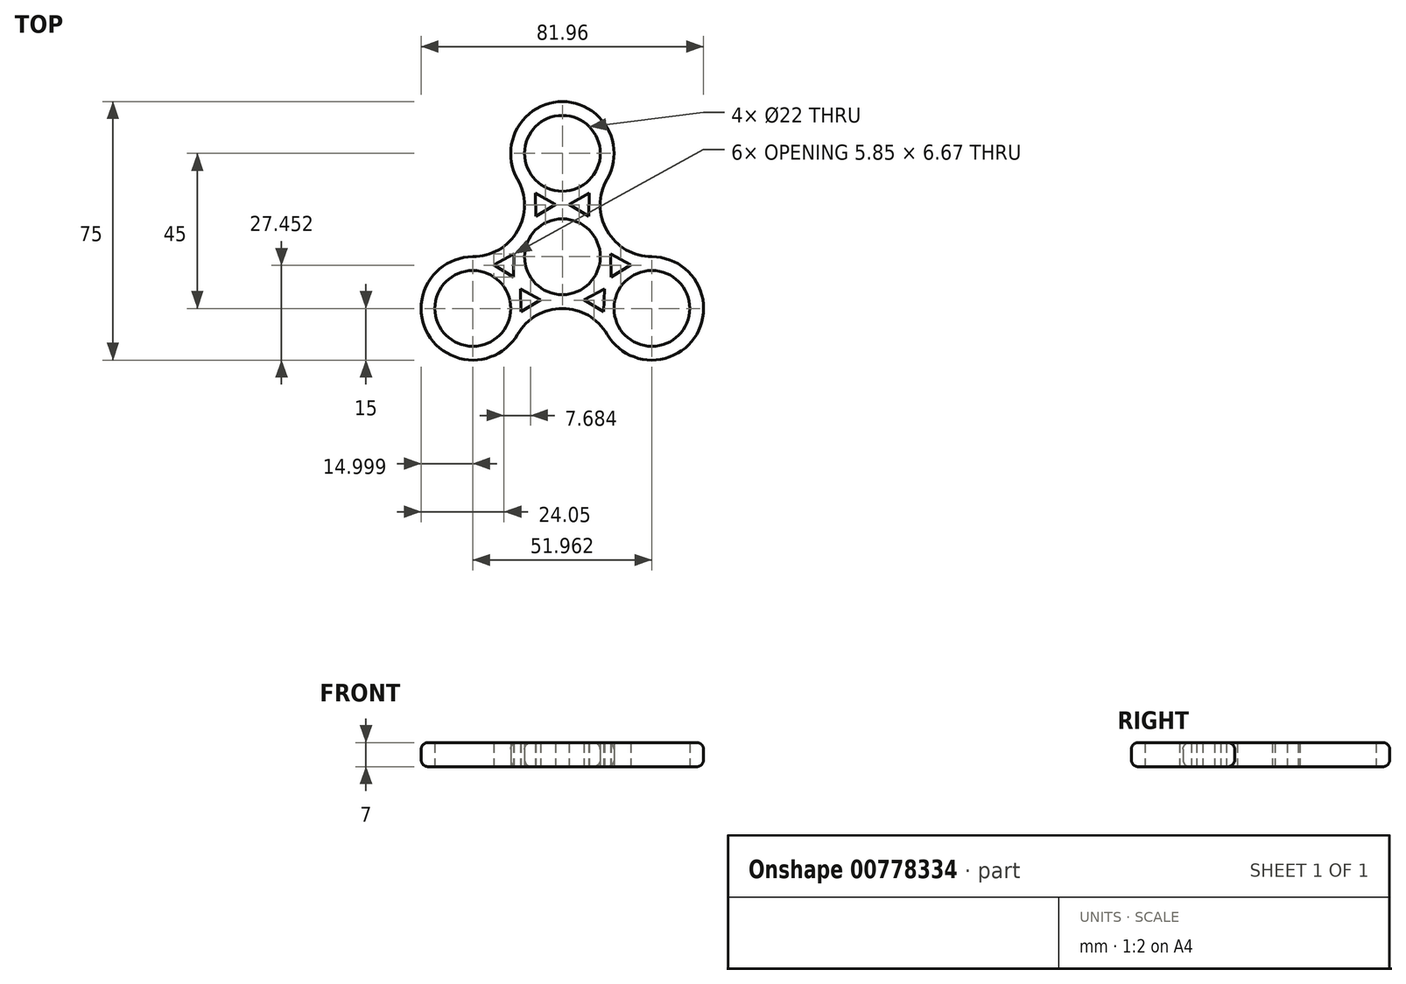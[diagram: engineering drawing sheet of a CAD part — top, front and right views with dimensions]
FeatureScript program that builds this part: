
annotation { "Feature Type Name" : "Feature", "Feature Type Description" : "" }
export const myFeature = defineFeature(function(context is Context, id is Id, definition is map)
    precondition{}
    {
        {
            var Q0;
            Q0=qCreatedBy(makeId("Top.planeOp"),FACE);
            var sketch = newSketch(context, id + "F0", { "sketchPlane" : qUnion([Q0])});
            skCircle(sketch, "E0", {"center": v(0, 0) * mm, "radius": 11 * mm});
            skCircle(sketch, "E1", {"center": v(0, 30) * mm, "radius": 11 * mm});
            skCircle(sketch, "E2", {"center": v(0, 0) * mm, "radius": 30 * mm, "construction": true});
            skLineSegment(sketch, "E3.0", {"start": v(0, 30) * mm, "end": v(25.98, -15) * mm, "construction": true});
            skLineSegment(sketch, "E3.1", {"start": v(25.98, -15) * mm, "end": v(-25.98, -15) * mm, "construction": true});
            skLineSegment(sketch, "E3.2", {"start": v(-25.98, -15) * mm, "end": v(0, 30) * mm, "construction": true});
            skCircle(sketch, "E4", {"center": v(-25.98, -15) * mm, "radius": 11 * mm});
            skCircle(sketch, "E5", {"center": v(25.98, -15) * mm, "radius": 11 * mm});
            skCircle(sketch, "E6", {"center": v(0, 0) * mm, "radius": 15 * mm, "construction": true});
            skArc(sketch, "E7", {"start": v(13, 22.5) * mm, "mid": v(0, 45) * mm, "end": v(-13, 22.5) * mm});
            skArc(sketch, "E8", {"start": v(13, -22.5) * mm, "mid": v(38.97, -22.5) * mm, "end": v(25.98, 0) * mm});
            skArc(sketch, "E9", {"start": v(-25.98, 0) * mm, "mid": v(-38.97, -22.5) * mm, "end": v(-13, -22.5) * mm});
            skArc(sketch, "E10", {"start": v(-25.98, 0) * mm, "mid": v(-13, 7.5) * mm, "end": v(-13, 22.5) * mm});
            skLineSegment(sketch, "E11", {"start": v(25.98, -15) * mm, "end": v(0, 0) * mm, "construction": true});
            skLineSegment(sketch, "E12", {"start": v(0, 0) * mm, "end": v(-35.55, 20.52) * mm, "construction": true});
            skLineSegment(sketch, "E13", {"start": v(-25.98, -15) * mm, "end": v(0, 0) * mm, "construction": true});
            skLineSegment(sketch, "E14", {"start": v(0, 0) * mm, "end": v(34.88, 20.14) * mm, "construction": true});
            skArc(sketch, "E15", {"start": v(13, 22.5) * mm, "mid": v(13, 7.5) * mm, "end": v(25.98, 0) * mm});
            skArc(sketch, "E16", {"start": v(13, -22.5) * mm, "mid": v(0, -15) * mm, "end": v(-13, -22.5) * mm});
            skCircle(sketch, "E17", {"center": v(0, 0) * mm, "radius": 16.75 * mm, "construction": true});
            skLineSegment(sketch, "E18.0", {"start": v(-7.83, 18.4) * mm, "end": v(-1.98, 15.2) * mm});
            skLineSegment(sketch, "E18.1", {"start": v(-1.98, 15.2) * mm, "end": v(-7.68, 11.74) * mm});
            skLineSegment(sketch, "E18.2", {"start": v(-7.68, 11.74) * mm, "end": v(-7.83, 18.4) * mm});
            skPoint(sketch, "E19.orphan", {"position": v(1.38, 16.14) * mm});
            skPoint(sketch, "E20.orphan", {"position": v(14.66, -6.88) * mm});
            skPoint(sketch, "E21.orphan", {"position": v(13.29, -9.26) * mm});
            skPoint(sketch, "E22.orphan", {"position": v(-14.66, -6.88) * mm});
            skPoint(sketch, "E23.orphan", {"position": v(-13.29, -9.26) * mm});
            skLineSegment(sketch, "E24.MirrorCS", {"start": v(7.83, 18.4) * mm, "end": v(1.98, 15.2) * mm});
            skLineSegment(sketch, "E25.MirrorCS", {"start": v(7.68, 11.74) * mm, "end": v(7.83, 18.4) * mm});
            skLineSegment(sketch, "E26.MirrorCS", {"start": v(1.98, 15.2) * mm, "end": v(7.68, 11.74) * mm});
            skLineSegment(sketch, "E27.MirrorCS", {"start": v(14, 0.79) * mm, "end": v(19.85, -2.42) * mm});
            skLineSegment(sketch, "E28.MirrorCS", {"start": v(14.15, -5.88) * mm, "end": v(14, 0.79) * mm});
            skLineSegment(sketch, "E29.MirrorCS", {"start": v(19.85, -2.42) * mm, "end": v(14.15, -5.88) * mm});
            skLineSegment(sketch, "E30.MirrorCS", {"start": v(12.17, -9.31) * mm, "end": v(6.32, -12.52) * mm});
            skLineSegment(sketch, "E31.MirrorCS", {"start": v(12.03, -15.98) * mm, "end": v(12.17, -9.31) * mm});
            skLineSegment(sketch, "E32.MirrorCS", {"start": v(6.32, -12.52) * mm, "end": v(12.03, -15.98) * mm});
            skLineSegment(sketch, "E33.MirrorCS", {"start": v(-14.15, -5.88) * mm, "end": v(-14, 0.79) * mm});
            skLineSegment(sketch, "E34.MirrorCS", {"start": v(-14, 0.79) * mm, "end": v(-19.85, -2.42) * mm});
            skLineSegment(sketch, "E35.MirrorCS", {"start": v(-19.85, -2.42) * mm, "end": v(-14.15, -5.88) * mm});
            skLineSegment(sketch, "E36.MirrorCS", {"start": v(-12.17, -9.31) * mm, "end": v(-6.32, -12.52) * mm});
            skLineSegment(sketch, "E37.MirrorCS", {"start": v(-12.03, -15.98) * mm, "end": v(-12.17, -9.31) * mm});
            skLineSegment(sketch, "E38.MirrorCS", {"start": v(-6.32, -12.52) * mm, "end": v(-12.03, -15.98) * mm});
            skSolve(sketch);
        }
        {
            var Q0;
            Q0=makeQuery(id+"F0.imprint","IMPRINT",FACE,{"disambiguationData":[TD([[makeQuery(id+"F0.imprint","IMPRINT",EDGE,{"derivedFrom":sQuery(id+"F0.wireOp",EDGE,"E0")}),-1.0]])]});
            extrude(context, id + "F1", {"entities" : qUnion([Q0]), "depth" : 7 * mm, "offsetDistance" : 25 * mm});
        }
        {
            var Q0;
            Q0=makeQuery(id+"F1.opExtrude","CAP_EDGE",EDGE,{"disambiguationData":[OSD([sQuery(id+"F0.wireOp",EDGE,"E10")])],"isStart":false});
            var Q1;
            Q1=makeQuery(id+"F1.opExtrude","CAP_EDGE",EDGE,{"disambiguationData":[OSD([sQuery(id+"F0.wireOp",EDGE,"E7")])],"isStart":false});
            var Q2;
            Q2=makeQuery(id+"F1.opExtrude","CAP_EDGE",EDGE,{"disambiguationData":[OSD([sQuery(id+"F0.wireOp",EDGE,"E15")])],"isStart":true});
            var Q3;
            Q3=makeQuery(id+"F1.opExtrude","CAP_EDGE",EDGE,{"disambiguationData":[OSD([sQuery(id+"F0.wireOp",EDGE,"E15")])],"isStart":false});
            var Q4;
            Q4=makeQuery(id+"F1.opExtrude","CAP_EDGE",EDGE,{"disambiguationData":[OSD([sQuery(id+"F0.wireOp",EDGE,"E8")])],"isStart":false});
            var Q5;
            Q5=makeQuery(id+"F1.opExtrude","CAP_EDGE",EDGE,{"disambiguationData":[OSD([sQuery(id+"F0.wireOp",EDGE,"E16")])],"isStart":false});
            var Q6;
            Q6=makeQuery(id+"F1.opExtrude","CAP_EDGE",EDGE,{"disambiguationData":[OSD([sQuery(id+"F0.wireOp",EDGE,"E9")])],"isStart":false});
            var Q7;
            Q7=makeQuery(id+"F1.opExtrude","CAP_EDGE",EDGE,{"disambiguationData":[OSD([sQuery(id+"F0.wireOp",EDGE,"E7")])],"isStart":true});
            var Q8;
            Q8=makeQuery(id+"F1.opExtrude","CAP_EDGE",EDGE,{"disambiguationData":[OSD([sQuery(id+"F0.wireOp",EDGE,"E10")])],"isStart":true});
            var Q9;
            Q9=makeQuery(id+"F1.opExtrude","CAP_EDGE",EDGE,{"disambiguationData":[OSD([sQuery(id+"F0.wireOp",EDGE,"E9")])],"isStart":true});
            var Q10;
            Q10=makeQuery(id+"F1.opExtrude","CAP_EDGE",EDGE,{"disambiguationData":[OSD([sQuery(id+"F0.wireOp",EDGE,"E16")])],"isStart":true});
            var Q11;
            Q11=makeQuery(id+"F1.opExtrude","CAP_EDGE",EDGE,{"disambiguationData":[OSD([sQuery(id+"F0.wireOp",EDGE,"E8")])],"isStart":true});
            fillet(context, id + "F2", {"entities" : qUnion([Q0, Q1, Q2, Q3, Q4, Q5, Q6, Q7, Q8, Q9, Q10, Q11]), "radius" : 2 * mm, "tangentPropagation" : true, "allowEdgeOverflow" : false});
        }
    });
